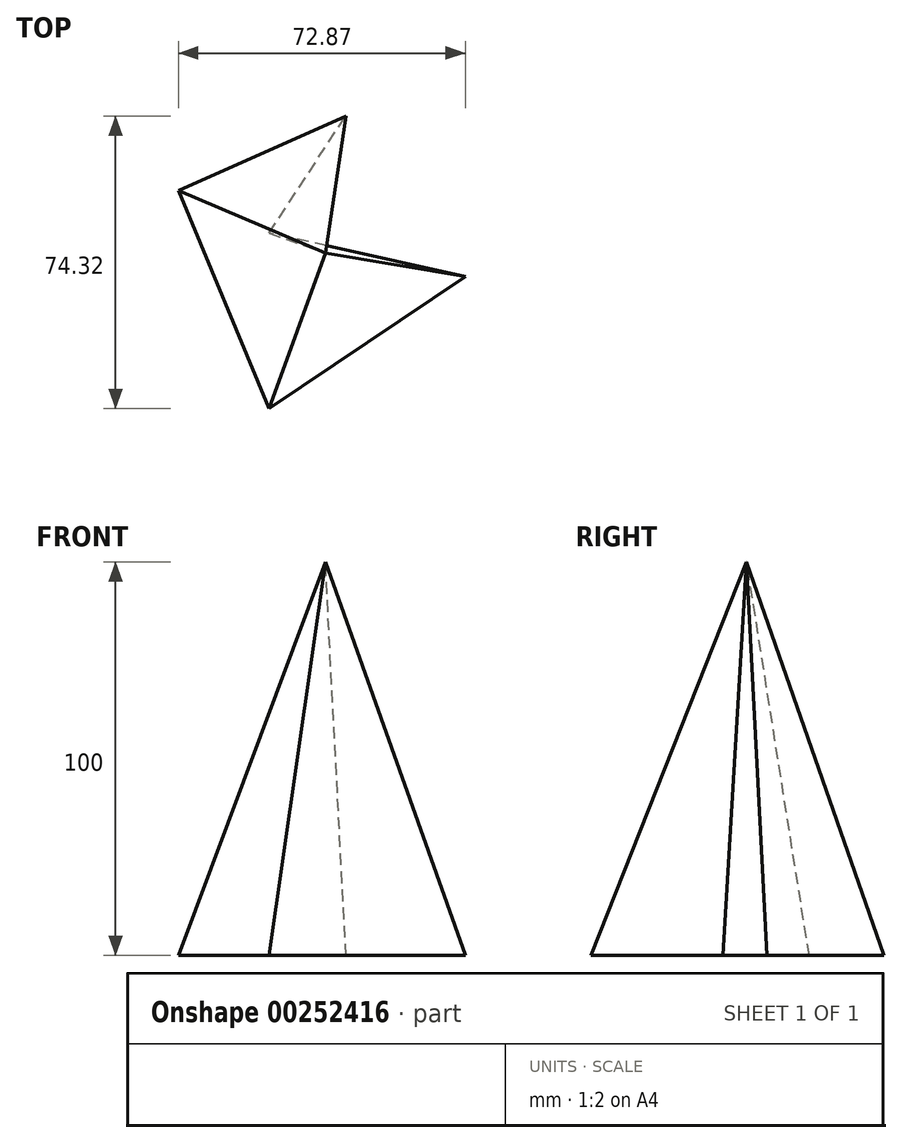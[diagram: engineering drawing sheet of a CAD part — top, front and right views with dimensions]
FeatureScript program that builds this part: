
annotation { "Feature Type Name" : "Feature", "Feature Type Description" : "" }
export const myFeature = defineFeature(function(context is Context, id is Id, definition is map)
    precondition{}
    {
        {
            var Q0;
            Q0=qCreatedBy(makeId("Top.planeOp"),FACE);
            var sketch = newSketch(context, id + "F0", { "sketchPlane" : qUnion([Q0])});
            skLineSegment(sketch, "E0", {"start": v(-37.3, 15.89) * mm, "end": v(-14.28, -39.5) * mm});
            skLineSegment(sketch, "E1", {"start": v(-14.28, -39.5) * mm, "end": v(35.56, -5.98) * mm});
            skLineSegment(sketch, "E2", {"start": v(35.56, -5.98) * mm, "end": v(-14.28, 5.1) * mm});
            skLineSegment(sketch, "E3", {"start": v(-14.28, 5.1) * mm, "end": v(5.25, 34.83) * mm});
            skLineSegment(sketch, "E4", {"start": v(5.25, 34.83) * mm, "end": v(-37.3, 15.89) * mm});
            skSolve(sketch);
        }
        {
            var Q0;
            Q0=qCreatedBy(makeId("Top.planeOp"),FACE);
            cPlane(context, id + "F1", {"entities" : qUnion([Q0]), "cplaneType" : CPlaneType.OFFSET, "offset" : 100 * mm, "width" : 152.4 * mm, "height" : 152.4 * mm});
        }
        {
            var Q0;
            Q0=qCreatedBy(id+"F1.planeOp",FACE);
            var sketch = newSketch(context, id + "F2", { "sketchPlane" : qUnion([Q0])});
            skPoint(sketch, "E5", {"position": v(0, 0) * mm});
            skSolve(sketch);
        }
        {
            var Q0;
            Q0=makeQuery(id+"F0.imprint","IMPRINT",FACE,{"disambiguationData":[TD([[makeQuery(id+"F0.imprint","IMPRINT",EDGE,{"derivedFrom":sQuery(id+"F0.wireOp",EDGE,"E0")}),1.0]])]});
            var Q1;
            Q1=sQuery(id+"F2.wireOp",VERTEX,"E5");
            loft(context, id + "F3", {"sheetProfilesArray" : [{ "sheetProfileEntities" : qUnion([Q0]) }, { "sheetProfileEntities" : qUnion([Q1]) }]});
        }
    });
